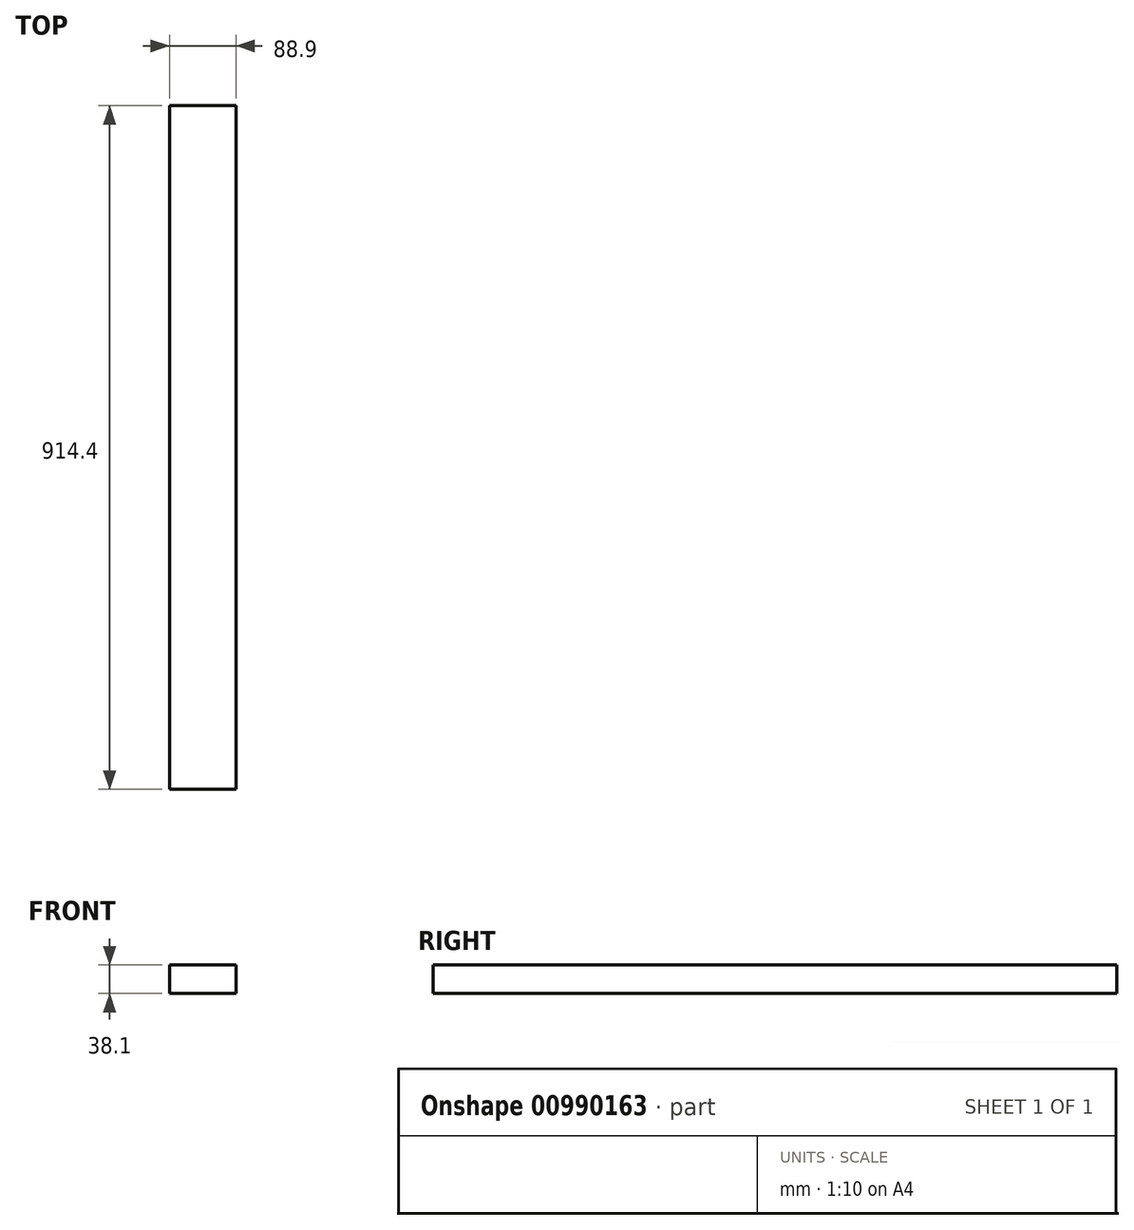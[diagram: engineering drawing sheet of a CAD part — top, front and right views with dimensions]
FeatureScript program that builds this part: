
annotation { "Feature Type Name" : "Feature", "Feature Type Description" : "" }
export const myFeature = defineFeature(function(context is Context, id is Id, definition is map)
    precondition{}
    {
        {
            assignVariable(context, id + "F0", {"name" : "w", "anyValue" : 38.1 * mm});
        }
        {
            var Q0;
            Q0=qCreatedBy(makeId("Top.planeOp"),FACE);
            var sketch = newSketch(context, id + "F1", { "sketchPlane" : qUnion([Q0])});
            skLineSegment(sketch, "E0.bottom", {"start": v(44.45, 457.2) * mm, "end": v(-44.45, 457.2) * mm});
            skLineSegment(sketch, "E0.top", {"start": v(44.45, -457.2) * mm, "end": v(-44.45, -457.2) * mm});
            skLineSegment(sketch, "E0.left", {"start": v(44.45, 457.2) * mm, "end": v(44.45, -457.2) * mm});
            skLineSegment(sketch, "E0.right", {"start": v(-44.45, 457.2) * mm, "end": v(-44.45, -457.2) * mm});
            skPoint(sketch, "E0.middle", {"position": v(0, 0) * mm});
            skSolve(sketch);
        }
        {
            var Q0;
            Q0=qSketchRegion(id+"F1",true);
            extrude(context, id + "F2", {"entities" : qUnion([Q0]), "depth" : getVariable(context, 'w'), "offsetDistance" : 25.4 * mm});
        }
    });
